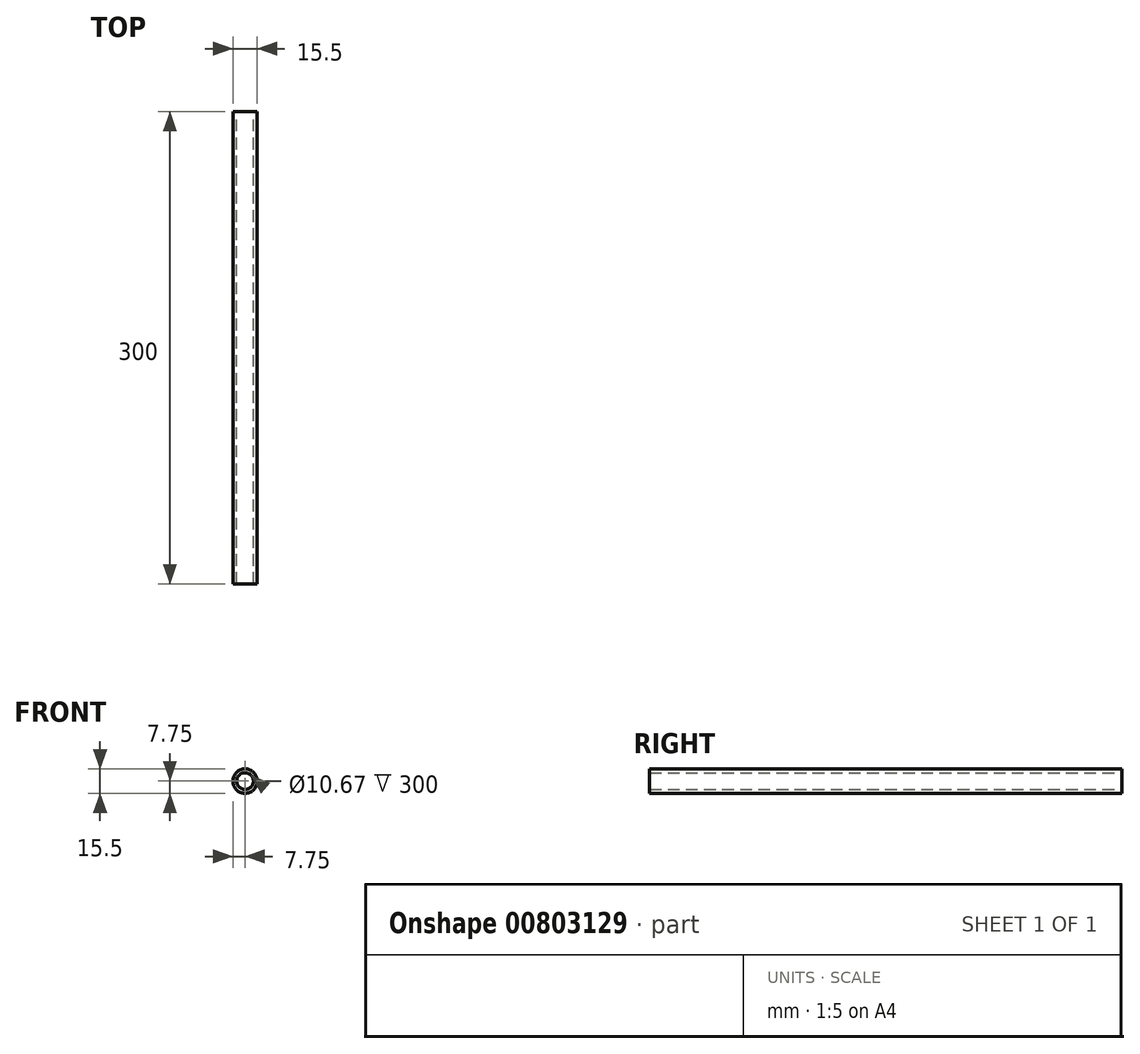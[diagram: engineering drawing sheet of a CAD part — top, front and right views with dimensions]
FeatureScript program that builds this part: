
annotation { "Feature Type Name" : "Feature", "Feature Type Description" : "" }
export const myFeature = defineFeature(function(context is Context, id is Id, definition is map)
    precondition{}
    {
        {
            var Q0;
            Q0=qCreatedBy(makeId("Front.planeOp"),FACE);
            var sketch = newSketch(context, id + "F0", { "sketchPlane" : qUnion([Q0])});
            skCircle(sketch, "E0", {"center": v(0, 0) * mm, "radius": 7.75 * mm});
            skCircle(sketch, "E1", {"center": v(0, 0) * mm, "radius": 5.33 * mm});
            skSolve(sketch);
        }
        {
            var Q0;
            Q0 = qSketchRegion(id + "F0", true);
            extrude(context, id + "F1", {"entities" : qUnion([Q0]), "depth" : 300 * mm, "offsetDistance" : 25 * mm});
        }
    });
